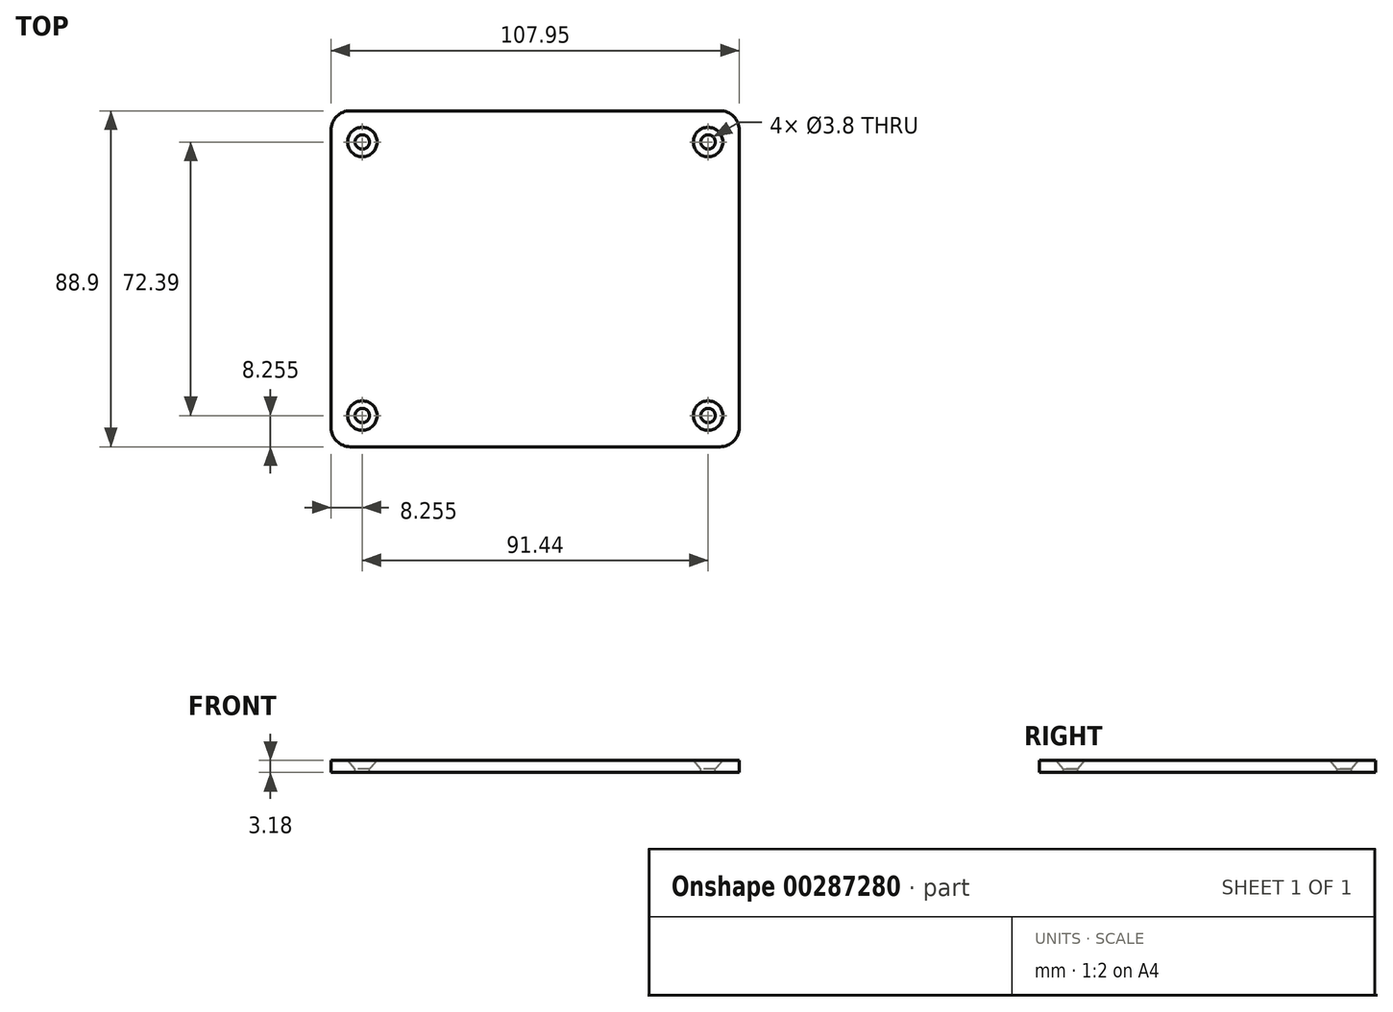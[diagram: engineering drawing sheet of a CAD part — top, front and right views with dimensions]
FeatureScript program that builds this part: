
annotation { "Feature Type Name" : "Feature", "Feature Type Description" : "" }
export const myFeature = defineFeature(function(context is Context, id is Id, definition is map)
    precondition{}
    {
        {
            var Q0;
            Q0=qCreatedBy(makeId("Top.planeOp"),FACE);
            var sketch = newSketch(context, id + "F0", { "sketchPlane" : qUnion([Q0])});
            skLineSegment(sketch, "E0.bottom", {"start": v(0, 0) * mm, "end": v(107.95, 0) * mm});
            skLineSegment(sketch, "E0.top", {"start": v(0, 88.9) * mm, "end": v(107.95, 88.9) * mm});
            skLineSegment(sketch, "E0.left", {"start": v(0, 0) * mm, "end": v(0, 88.9) * mm});
            skLineSegment(sketch, "E0.right", {"start": v(107.95, 0) * mm, "end": v(107.95, 88.9) * mm});
            skSolve(sketch);
        }
        {
            var Q0;
            Q0 = qSketchRegion(id + "F0", true);
            extrude(context, id + "F1", {"entities" : qUnion([Q0]), "depth" : 3.17 * mm});
        }
        {
            var Q0;
            Q0=makeQuery(id+"F1.opExtrude","CAP_FACE",FACE,{"disambiguationData":[OSD([sQuery(id+"F0.wireOp",EDGE,"E0.bottom"),sQuery(id+"F0.wireOp",EDGE,"E0.top"),sQuery(id+"F0.wireOp",EDGE,"E0.left"),sQuery(id+"F0.wireOp",EDGE,"E0.right")])],"isStart":false});
            var sketch = newSketch(context, id + "F2", { "sketchPlane" : qUnion([Q0])});
            skLineSegment(sketch, "E1", {"start": v(53.97, 88.9) * mm, "end": v(53.98, 0) * mm, "construction": true});
            skLineSegment(sketch, "E2", {"start": v(0, 44.45) * mm, "end": v(107.95, 44.45) * mm, "construction": true});
            skPoint(sketch, "E3", {"position": v(8.25, 80.65) * mm});
            skPoint(sketch, "E4", {"position": v(99.7, 80.65) * mm});
            skPoint(sketch, "E5", {"position": v(99.7, 8.26) * mm});
            skPoint(sketch, "E6", {"position": v(8.26, 8.26) * mm});
            skSolve(sketch);
        }
        {
            var Q0;
            Q0=sQuery(id+"F2.wireOp",VERTEX,"E3");
            var Q1;
            Q1=sQuery(id+"F2.wireOp",VERTEX,"E4");
            var Q2;
            Q2=sQuery(id+"F2.wireOp",VERTEX,"E5");
            var Q3;
            Q3=sQuery(id+"F2.wireOp",VERTEX,"E6");
            var Q4;
            Q4=makeQuery(id+"F1.opExtrude","SWEPT_BODY",BODY,{"disambiguationData":[OSD([sQuery(id+"F0.wireOp",EDGE,"E0.bottom"),sQuery(id+"F0.wireOp",EDGE,"E0.top"),sQuery(id+"F0.wireOp",EDGE,"E0.left"),sQuery(id+"F0.wireOp",EDGE,"E0.right")])]});
            hole(context, id + "F3", {"style" : HoleStyle.C_SINK, "endStyle" : HoleEndStyle.THROUGH, "standardTappedOrClearance" : lookupTablePath({ "standard" : "ANSI", "fit" : "Normal (ASME)", "size" : "#6", "type" : "Clearance" }), "standardBlindInLast" : lookupTablePath({ "fit" : "Free", "standard" : "ANSI", "size" : "#6", "type" : "Clearance" }), "holeDiameter" : 3.8 * mm, "cSinkDiameter" : 7.8 * mm, "cSinkAngle" : 82 * degree, "tappedDepth" : 2.77 * mm, "tapClearance" : 3, "startFromSketch" : true, "locations" : qUnion([Q0, Q1, Q2, Q3]), "scope" : qUnion([Q4])});
        }
        {
            var Q0;
            Q0=makeQuery(id+"F1.opExtrude","SWEPT_EDGE",EDGE,{"disambiguationData":[OSD([sQuery(id+"F0.wireOp",EDGE,"E0.bottom"),sQuery(id+"F0.wireOp",EDGE,"E0.left")])]});
            var Q1;
            Q1=makeQuery(id+"F1.opExtrude","SWEPT_EDGE",EDGE,{"disambiguationData":[OSD([sQuery(id+"F0.wireOp",EDGE,"E0.bottom"),sQuery(id+"F0.wireOp",EDGE,"E0.right")])]});
            var Q2;
            Q2=makeQuery(id+"F1.opExtrude","SWEPT_EDGE",EDGE,{"disambiguationData":[OSD([sQuery(id+"F0.wireOp",EDGE,"E0.top"),sQuery(id+"F0.wireOp",EDGE,"E0.right")])]});
            var Q3;
            Q3=makeQuery(id+"F1.opExtrude","SWEPT_EDGE",EDGE,{"disambiguationData":[OSD([sQuery(id+"F0.wireOp",EDGE,"E0.top"),sQuery(id+"F0.wireOp",EDGE,"E0.left")])]});
            fillet(context, id + "F4", {"entities" : qUnion([Q0, Q1, Q2, Q3]), "radius" : 5.08 * mm, "tangentPropagation" : true, "allowEdgeOverflow" : false});
        }
    });
